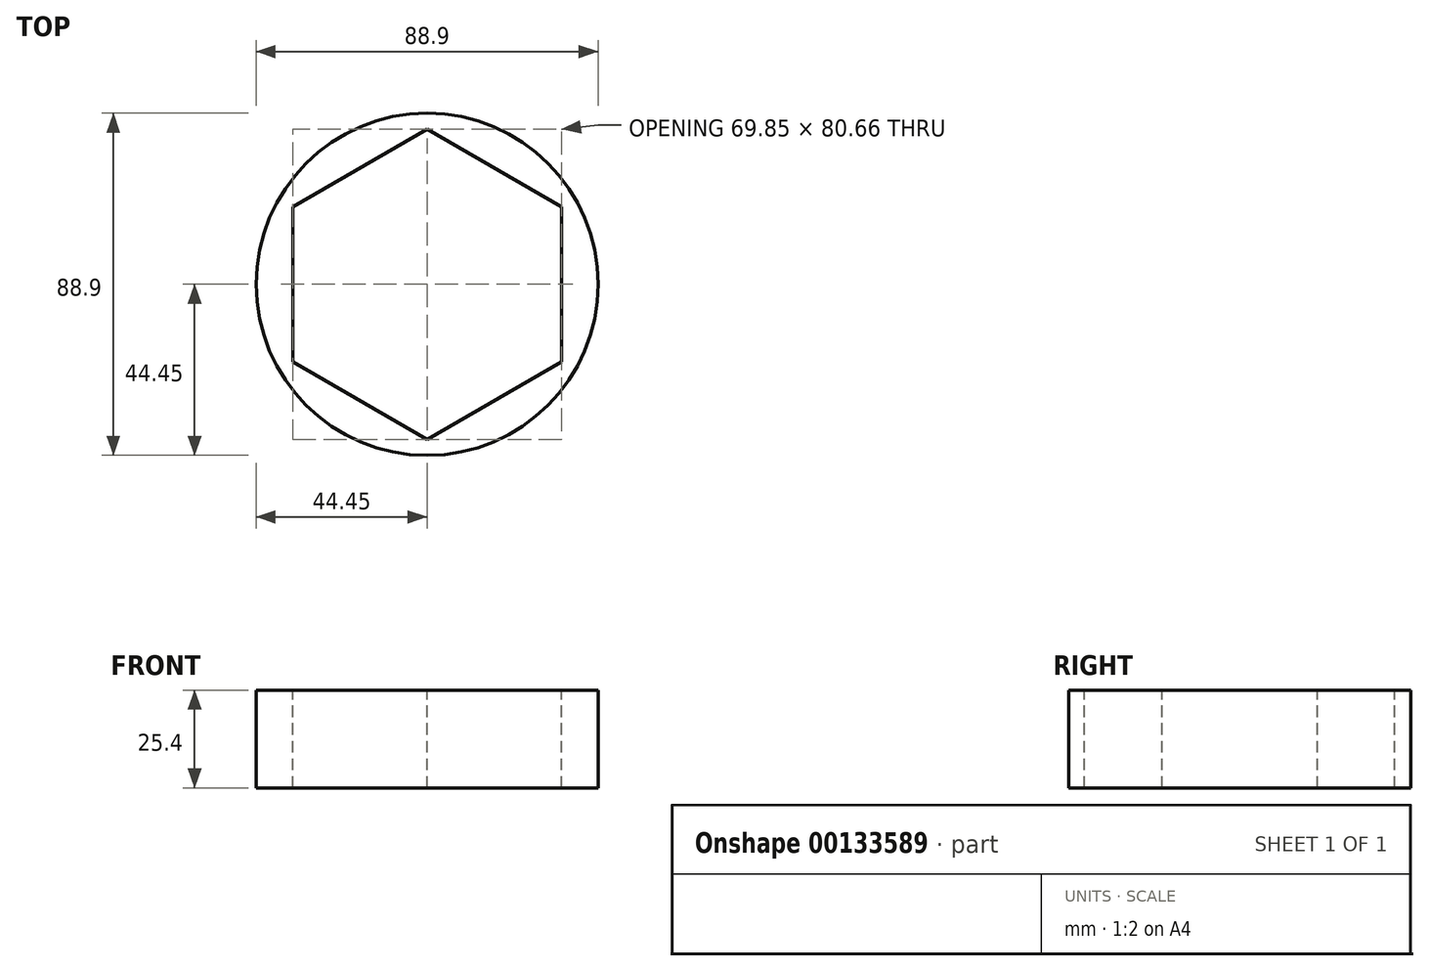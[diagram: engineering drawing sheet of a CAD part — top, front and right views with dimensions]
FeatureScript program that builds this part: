
annotation { "Feature Type Name" : "Feature", "Feature Type Description" : "" }
export const myFeature = defineFeature(function(context is Context, id is Id, definition is map)
    precondition{}
    {
        {
            var Q0;
            Q0=qCreatedBy(makeId("Top.planeOp"),FACE);
            var sketch = newSketch(context, id + "F0", { "sketchPlane" : qUnion([Q0])});
            skCircle(sketch, "E0", {"center": v(0, 0) * mm, "radius": 44.45 * mm});
            skCircle(sketch, "E1.cCircle", {"center": v(0, 0) * mm, "radius": 34.93 * mm, "construction": true});
            skLineSegment(sketch, "E1.0", {"start": v(34.93, 20.16) * mm, "end": v(34.93, -20.16) * mm});
            skLineSegment(sketch, "E1.1", {"start": v(34.93, -20.16) * mm, "end": v(0, -40.33) * mm});
            skLineSegment(sketch, "E1.2", {"start": v(0, -40.33) * mm, "end": v(-34.92, -20.16) * mm});
            skLineSegment(sketch, "E1.3", {"start": v(-34.92, -20.16) * mm, "end": v(-34.93, 20.16) * mm});
            skLineSegment(sketch, "E1.4", {"start": v(-34.93, 20.16) * mm, "end": v(0, 40.33) * mm});
            skLineSegment(sketch, "E1.5", {"start": v(0, 40.33) * mm, "end": v(34.93, 20.16) * mm});
            skPoint(sketch, "E1.0.midPoint", {"position": v(34.93, 0) * mm});
            skSolve(sketch);
        }
        {
            var Q0;
            Q0=makeQuery(id+"F0.imprint","IMPRINT",FACE,{"disambiguationData":[TD([[makeQuery(id+"F0.imprint","IMPRINT",EDGE,{"derivedFrom":sQuery(id+"F0.wireOp",EDGE,"E0")}),1.0]])]});
            extrude(context, id + "F1", {"entities" : qUnion([Q0]), "oppositeDirection" : true, "depth" : 25.4 * mm});
        }
    });
